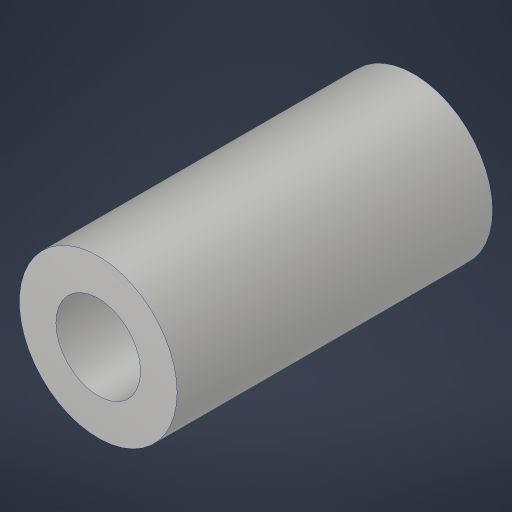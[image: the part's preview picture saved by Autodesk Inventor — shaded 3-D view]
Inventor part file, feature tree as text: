
AUTODESK INVENTOR PART (.ipt)
format: ipt  version: 2023.4 (Build 274418000, 418)  size: 171,008 bytes
history: native  units: in
note: dims shown in document units (in); Inventor stores cm internally (conversion verified against a paired STEP export)
features: extrude x1, hole x1
ambient origin geometry x8: Origin, YZ Plane, XZ Plane, XY Plane, X Axis, Y Axis, Z Axis, Center Point
bodies: Solid1 (feature_tree)
feature tree (2):
  extrude  "Extrusion1"  Depth=0.75in
  hole  "Hole1"  [1 undecoded]
note: 1 required parameter value undecoded (feature->parameter linkage not recoverable at this tier; creation-order binding heuristic only, values carry confidence <= 0.55)
